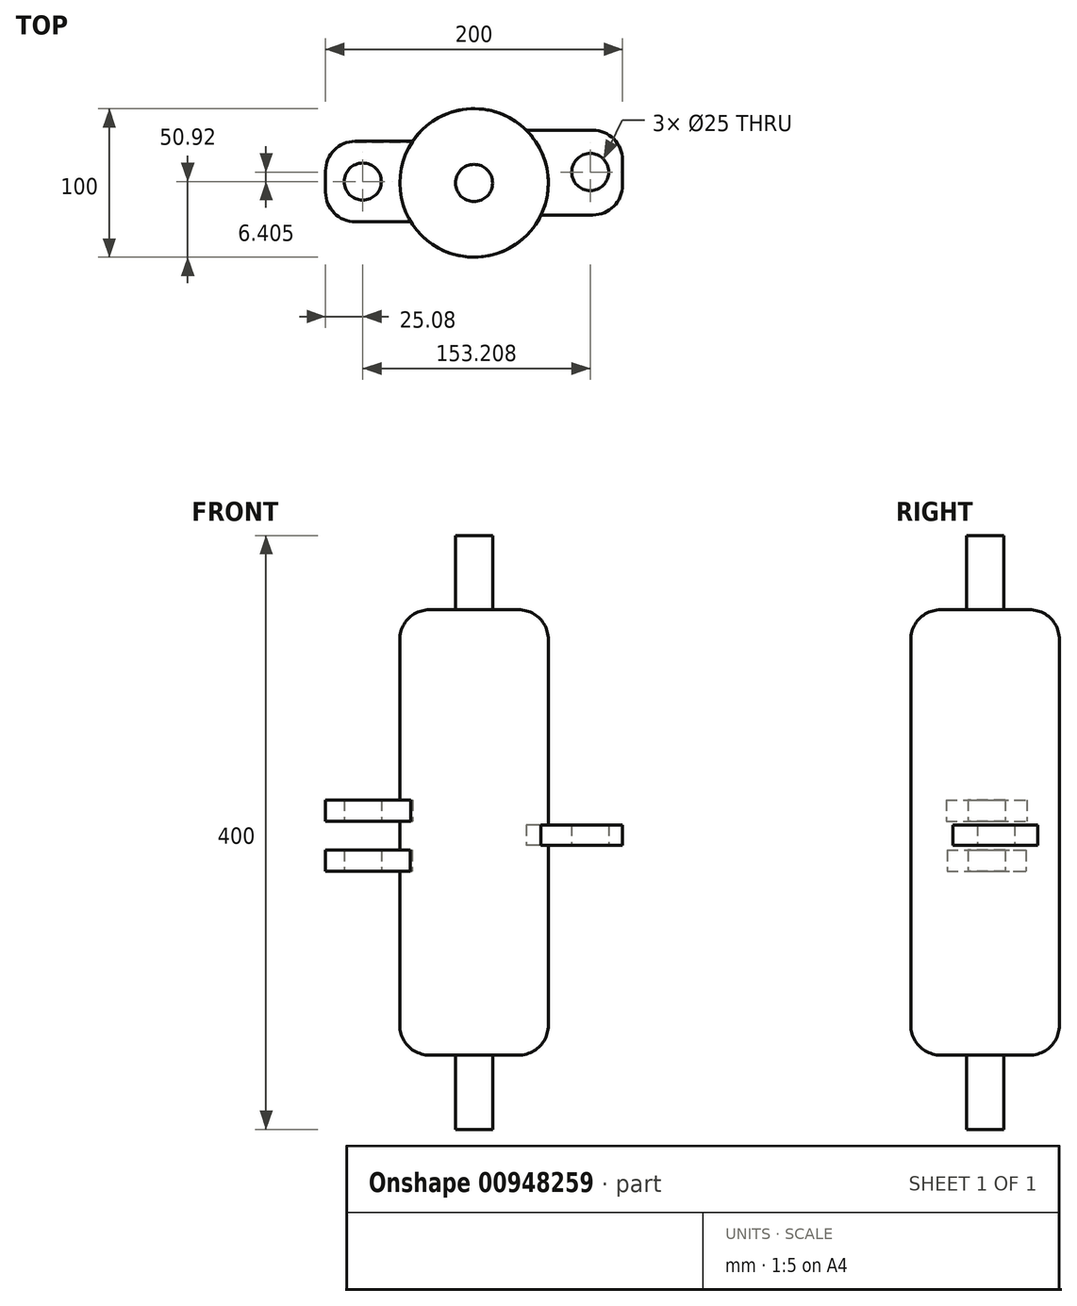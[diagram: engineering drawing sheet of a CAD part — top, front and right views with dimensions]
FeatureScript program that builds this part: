
annotation { "Feature Type Name" : "Feature", "Feature Type Description" : "" }
export const myFeature = defineFeature(function(context is Context, id is Id, definition is map)
    precondition{}
    {
        {
            var Q0;
            Q0=qCreatedBy(makeId("Top.planeOp"),FACE);
            var sketch = newSketch(context, id + "F0", { "sketchPlane" : qUnion([Q0])});
            skCircle(sketch, "E0", {"center": v(0, 0) * mm, "radius": 50 * mm});
            skSolve(sketch);
        }
        {
            var Q0;
            Q0=makeQuery(id+"F0.imprint","IMPRINT",FACE,{"disambiguationData":[TD([[makeQuery(id+"F0.imprint","IMPRINT",EDGE,{"derivedFrom":sQuery(id+"F0.wireOp",EDGE,"E0")}),1.0]])]});
            extrude(context, id + "F1", {"entities" : qUnion([Q0]), "depth" : 300 * mm, "offsetDistance" : 25 * mm});
        }
        {
            var Q0;
            Q0=qCreatedBy(makeId("Right.planeOp"),FACE);
            var sketch = newSketch(context, id + "F2", { "sketchPlane" : qUnion([Q0])});
            skLineSegment(sketch, "E1.bottom", {"start": v(-26.2, 171.85) * mm, "end": v(28.05, 171.85) * mm});
            skLineSegment(sketch, "E1.top", {"start": v(-26.2, 157.4) * mm, "end": v(28.05, 157.4) * mm});
            skLineSegment(sketch, "E1.left", {"start": v(-26.2, 171.85) * mm, "end": v(-26.2, 157.4) * mm});
            skLineSegment(sketch, "E1.right", {"start": v(28.05, 171.85) * mm, "end": v(28.05, 157.4) * mm});
            skLineSegment(sketch, "E2.bottom", {"start": v(-25.58, 138.14) * mm, "end": v(27.42, 138.14) * mm});
            skLineSegment(sketch, "E2.top", {"start": v(-25.58, 123.97) * mm, "end": v(27.42, 123.97) * mm});
            skLineSegment(sketch, "E2.left", {"start": v(-25.58, 138.14) * mm, "end": v(-25.58, 123.97) * mm});
            skLineSegment(sketch, "E2.right", {"start": v(27.42, 138.14) * mm, "end": v(27.42, 123.97) * mm});
            skSolve(sketch);
        }
        {
            var Q0;
            Q0 = qSketchRegion(id + "F2", true);
            extrude(context, id + "F3", {"entities" : qUnion([Q0]), "operationType" : NewBodyOperationType.ADD, "oppositeDirection" : true, "depth" : 100 * mm, "offsetDistance" : 25 * mm});
        }
        {
            var Q0;
            Q0=qCreatedBy(makeId("Right.planeOp"),FACE);
            var sketch = newSketch(context, id + "F4", { "sketchPlane" : qUnion([Q0])});
            skLineSegment(sketch, "E3.bottom", {"start": v(-21.56, 155.05) * mm, "end": v(35.53, 155.05) * mm});
            skLineSegment(sketch, "E3.top", {"start": v(-21.56, 141.26) * mm, "end": v(35.53, 141.26) * mm});
            skLineSegment(sketch, "E3.left", {"start": v(-21.56, 155.05) * mm, "end": v(-21.56, 141.26) * mm});
            skLineSegment(sketch, "E3.right", {"start": v(35.53, 155.05) * mm, "end": v(35.53, 141.26) * mm});
            skSolve(sketch);
        }
        {
            var Q0;
            Q0=makeQuery(id+"F4.imprint","IMPRINT",FACE,{"disambiguationData":[TD([[makeQuery(id+"F4.imprint","IMPRINT",EDGE,{"derivedFrom":sQuery(id+"F4.wireOp",EDGE,"E3.bottom")}),-1.0]])]});
            extrude(context, id + "F5", {"entities" : qUnion([Q0]), "operationType" : NewBodyOperationType.ADD, "depth" : 100 * mm, "offsetDistance" : 25 * mm});
        }
        {
            var Q0;
            Q0=makeQuery(id+"F5.opExtrude","SWEPT_FACE",FACE,{"disambiguationData":[OSD([sQuery(id+"F4.wireOp",EDGE,"E3.top")])]});
            var sketch = newSketch(context, id + "F6", { "sketchPlane" : qUnion([Q0])});
            skCircle(sketch, "E4", {"center": v(78.29, -7.33) * mm, "radius": 12.5 * mm});
            skSolve(sketch);
        }
        {
            var Q0;
            Q0=makeQuery(id+"F6.imprint","IMPRINT",FACE,{"disambiguationData":[TD([[makeQuery(id+"F6.imprint","IMPRINT",EDGE,{"derivedFrom":sQuery(id+"F6.wireOp",EDGE,"E4")}),1.0]])]});
            extrude(context, id + "F7", {"entities" : qUnion([Q0]), "operationType" : NewBodyOperationType.REMOVE, "endBound" : BoundingType.THROUGH_ALL, "oppositeDirection" : true, "depth" : 25 * mm, "offsetDistance" : 25 * mm});
        }
        {
            var Q0;
            Q0=makeQuery(id+"F3.opExtrude","SWEPT_FACE",FACE,{"disambiguationData":[OSD([sQuery(id+"F2.wireOp",EDGE,"E2.top")])]});
            var sketch = newSketch(context, id + "F8", { "sketchPlane" : qUnion([Q0])});
            skCircle(sketch, "E5", {"center": v(-74.92, -0.92) * mm, "radius": 12.5 * mm});
            skPoint(sketch, "E5.centerSnap0", {"position": v(-100, -0.92) * mm});
            skSolve(sketch);
        }
        {
            var Q0;
            Q0=makeQuery(id+"F8.imprint","IMPRINT",FACE,{"disambiguationData":[TD([[makeQuery(id+"F8.imprint","IMPRINT",EDGE,{"derivedFrom":sQuery(id+"F8.wireOp",EDGE,"E5")}),1.0]])]});
            extrude(context, id + "F9", {"entities" : qUnion([Q0]), "operationType" : NewBodyOperationType.REMOVE, "endBound" : BoundingType.THROUGH_ALL, "oppositeDirection" : true, "depth" : 25 * mm, "offsetDistance" : 25 * mm});
        }
        {
            var Q0;
            Q0=makeQuery(id+"F1.opExtrude","CAP_EDGE",EDGE,{"disambiguationData":[OSD([sQuery(id+"F0.wireOp",EDGE,"E0")])],"isStart":false});
            var Q1;
            Q1=makeQuery(id+"F1.opExtrude","CAP_EDGE",EDGE,{"disambiguationData":[OSD([sQuery(id+"F0.wireOp",EDGE,"E0")])],"isStart":true});
            fillet(context, id + "F10", {"entities" : qUnion([Q0, Q1]), "radius" : 20 * mm, "tangentPropagation" : true, "allowEdgeOverflow" : false});
        }
        {
            var Q0;
            Q0=makeQuery(id+"FUfCV9SkS3nmhP0_1.opExtrude","CAP_EDGE",EDGE,{"disambiguationData":[OSD([sQuery(id+"FtyzQWb4Zui6vHR_1.wireOp",EDGE,"BCNSVXFy-DjdZ-V1KP-CNAp-fhgJUGBu6Xfa.left")])],"isStart":false});
            var Q1;
            Q1=makeQuery(id+"FUfCV9SkS3nmhP0_1.opExtrude","CAP_EDGE",EDGE,{"disambiguationData":[OSD([sQuery(id+"FtyzQWb4Zui6vHR_1.wireOp",EDGE,"DBq9CuZF-UmQ7-NoAr-yviu-CY6kCanwiIaz.left")])],"isStart":false});
            var Q2;
            Q2=makeQuery(id+"FUfCV9SkS3nmhP0_1.opExtrude","CAP_EDGE",EDGE,{"disambiguationData":[OSD([sQuery(id+"FtyzQWb4Zui6vHR_1.wireOp",EDGE,"DBq9CuZF-UmQ7-NoAr-yviu-CY6kCanwiIaz.right")])],"isStart":false});
            var Q3;
            Q3=makeQuery(id+"FUfCV9SkS3nmhP0_1.opExtrude","CAP_EDGE",EDGE,{"disambiguationData":[OSD([sQuery(id+"FtyzQWb4Zui6vHR_1.wireOp",EDGE,"BCNSVXFy-DjdZ-V1KP-CNAp-fhgJUGBu6Xfa.right")])],"isStart":false});
            var Q4;
            Q4=makeQuery(id+"F5.opExtrude","CAP_EDGE",EDGE,{"disambiguationData":[OSD([sQuery(id+"F4.wireOp",EDGE,"E3.right")])],"isStart":false});
            var Q5;
            Q5=makeQuery(id+"F5.opExtrude","CAP_EDGE",EDGE,{"disambiguationData":[OSD([sQuery(id+"F4.wireOp",EDGE,"E3.left")])],"isStart":false});
            var Q6;
            Q6=makeQuery(id+"F3.opExtrude","CAP_EDGE",EDGE,{"disambiguationData":[OSD([sQuery(id+"F2.wireOp",EDGE,"E2.left")])],"isStart":false});
            var Q7;
            Q7=makeQuery(id+"F3.opExtrude","CAP_EDGE",EDGE,{"disambiguationData":[OSD([sQuery(id+"F2.wireOp",EDGE,"E2.right")])],"isStart":false});
            var Q8;
            Q8=makeQuery(id+"F3.opExtrude","CAP_EDGE",EDGE,{"disambiguationData":[OSD([sQuery(id+"F2.wireOp",EDGE,"E1.left")])],"isStart":false});
            var Q9;
            Q9=makeQuery(id+"F3.opExtrude","CAP_EDGE",EDGE,{"disambiguationData":[OSD([sQuery(id+"F2.wireOp",EDGE,"E1.right")])],"isStart":false});
            var Q10;
            Q10=makeQuery(id+"FHOf3S6crCqmYKT_1.opExtrude","CAP_EDGE",EDGE,{"disambiguationData":[OSD([sQuery(id+"FLGOlIvUXUrBdLo_1.wireOp",EDGE,"xjBeedlk-bCSv-GhxD-SUAk-P5qBiVcfDNjS.right")])],"isStart":false});
            var Q11;
            Q11=makeQuery(id+"FHOf3S6crCqmYKT_1.opExtrude","CAP_EDGE",EDGE,{"disambiguationData":[OSD([sQuery(id+"FLGOlIvUXUrBdLo_1.wireOp",EDGE,"BlF1P5b0-vTRP-QuEt-POug-7c1wiY2q90gU.right")])],"isStart":false});
            var Q12;
            Q12=makeQuery(id+"FHOf3S6crCqmYKT_1.opExtrude","CAP_EDGE",EDGE,{"disambiguationData":[OSD([sQuery(id+"FLGOlIvUXUrBdLo_1.wireOp",EDGE,"xjBeedlk-bCSv-GhxD-SUAk-P5qBiVcfDNjS.left")])],"isStart":false});
            var Q13;
            Q13=makeQuery(id+"FHOf3S6crCqmYKT_1.opExtrude","CAP_EDGE",EDGE,{"disambiguationData":[OSD([sQuery(id+"FLGOlIvUXUrBdLo_1.wireOp",EDGE,"BlF1P5b0-vTRP-QuEt-POug-7c1wiY2q90gU.left")])],"isStart":false});
            fillet(context, id + "F11", {"entities" : qUnion([Q0, Q1, Q2, Q3, Q4, Q5, Q6, Q7, Q8, Q9, Q10, Q11, Q12, Q13]), "radius" : 20 * mm, "tangentPropagation" : true, "allowEdgeOverflow" : false});
        }
        {
            var Q0;
            Q0=makeQuery(id+"F1.opExtrude","CAP_FACE",FACE,{"disambiguationData":[OSD([sQuery(id+"F0.wireOp",EDGE,"E0")])],"isStart":false});
            var sketch = newSketch(context, id + "F12", { "sketchPlane" : qUnion([Q0])});
            skCircle(sketch, "E6", {"center": v(0, 0) * mm, "radius": 12.5 * mm});
            skSolve(sketch);
        }
        {
            var Q0;
            Q0=makeQuery(id+"F12.imprint","IMPRINT",FACE,{"disambiguationData":[TD([[makeQuery(id+"F12.imprint","IMPRINT",EDGE,{"derivedFrom":sQuery(id+"F12.wireOp",EDGE,"E6")}),1.0]])]});
            extrude(context, id + "F13", {"entities" : qUnion([Q0]), "operationType" : NewBodyOperationType.ADD, "depth" : 50 * mm, "offsetDistance" : 25 * mm});
        }
        {
            var Q0;
            Q0=makeQuery(id+"F1.opExtrude","CAP_FACE",FACE,{"disambiguationData":[OSD([sQuery(id+"F0.wireOp",EDGE,"E0")])],"isStart":true});
            var sketch = newSketch(context, id + "F14", { "sketchPlane" : qUnion([Q0])});
            skCircle(sketch, "E7", {"center": v(0, 0) * mm, "radius": 12.5 * mm});
            skSolve(sketch);
        }
        {
            var Q0;
            Q0=makeQuery(id+"F14.imprint","IMPRINT",FACE,{"disambiguationData":[TD([[makeQuery(id+"F14.imprint","IMPRINT",EDGE,{"derivedFrom":sQuery(id+"F14.wireOp",EDGE,"E7")}),1.0]])]});
            extrude(context, id + "F15", {"entities" : qUnion([Q0]), "operationType" : NewBodyOperationType.ADD, "depth" : 50 * mm, "offsetDistance" : 25 * mm});
        }
    });
